# Revit family: FireFighting_Tamper-Resistant-Dual-Hydrant-Valve-Cover_Galvin
name_source: partatom
category: Mechanical Equipment
revit_build: Autodesk Revit MEP 2012 (Build: 20110916_2132(x64)
units: mm (PartAtom-declared; Revit-internal decimal feet)

## types (1)
- 381331
    Assembly Code = D4030
    Description = Tamper Resistant Dual Hydrant Valve Cover (Painted)
    DimDepth = 220 mm  [stored 0.721785 ft]
    DimHeight = 220 mm  [stored 0.721785 ft]
    DimWidth = 420 mm  [stored 1.37795 ft]
    FilterObject_ANZRS = 381331
    Instructions = http://www.galvinengineering.com.au
    Keynote = 10520
    Manufacturer = Galvin Engineering
    Model = 381331
    ModifiedIssue_ANZRS = 20140330 $
    StyleOrType_ANZRS = Fire Fighting Equipment
    Type Comments = 381331
    URL = www.galvinengineering.com.au

note: [stored X ft] marks values corroborated as IEEE doubles in the binary element streams (Revit-internal decimal feet)

## geometry (parser evidence)
native form markers: Blend x2, Sweep x1
no freeform markers — native parametric forms only
